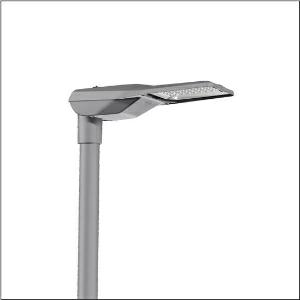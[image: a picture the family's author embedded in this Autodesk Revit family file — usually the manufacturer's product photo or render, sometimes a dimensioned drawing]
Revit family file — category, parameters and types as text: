
# Revit family: streetlight_sl_21_iq_mini___p0_5a_5xe2v31v08jb_ab6f
name_source: partatom
category: Lighting Fixtures
units: mm (PartAtom-declared; Revit-internal decimal feet)

## family parameters
Cut with Voids When Loaded = No
Host = Face
Light Source = No
Part Type = Normal
Room Calculation Point = No
Round Connector Dimension = Use Diameter
Shared = No

## types (1)
- --- (1 x LED, 11020 lm, 72.5 W, 3000K)
    Apparent Load = 73 VA
    CIE Flux Codes = 37 73 96 100 100
    Color Rendering = 70
    Color Temperature = 3000K
    Default Elevation = 1800 mm
    Description = Streetlight SL 21 iQ mini, mast luminaire, primary light control with lens, of PMMA, primary optical cover: cover, of toughened safety glass, transparent, light distribution: P0.5a, light emission: direct distribution, primary light characteristic: asymmetric, installation type: post-top, side-entry, LED, High Power LED, rated luminous flux: 11.020lm, luminous efficacy: 152lm/W, light colour: 730, colour temperature: 3000K, control gear: iQ-Street Remote, D4i with power reduction, control: pre-setting: logarithmic dimming characteristic, Street-Remote, Auto-Match, Temp-Guard, Lumen-Switch, Night-Set, Smart-Wire, Light-Fading, Desk-Remote (wireless, voltage-free reading and setting of iQ features in the workshop via application-optimized NFC function/RFID function), optimised constant luminous flux control (CLO 2.0), mains connection: 220..240V, AC, 50/60Hz, start of lifetime: 73W, end of service life: 76W, reduction: 33W, luminaire housing, of diecast aluminium, powder-coated, SITECO metallic grey (DB 702S), corrosivity category C5 high according to DIN EN ISO 12944, please order mast flange separately, inclination adjustable: 0°, 5°, 10°, 15°, sealing non-destructively replaceable, multi-level sealing system, length: 628mm, width: 235mm, height: 110mm, mast flange for spigot size: 42mm (side-entry): 5XC10008XM4, 60/48mm (side-entry/post-top): 5XC10108XM2, 76/60mm (side-entry/post-top): 5XC10108XM1, mounting height: 4..8m, Smart Interface above, protection rating (complete): IP66, insulation class (complete): insulation class II (safety insulation), certification: CE, ENEC, ENEC+, VDE, impact resistance: IK10, permissible operating ambient temperature for outdoor applications: -40..+50°C, standard-compliant lighting for roads and squares, packaging unit: 1 piece

Light Distribution: P0.5a
    Height = 110 mm
    Lamp = 1 x LED
    Lamp Light Flux = 11020 lm
    Lamp Power = 72.5 W
    Lamp count = 1
    Length = 625 mm
    Luminous efficacy = 152 lm/W
    Manufacturer = Siteco
    ModVariant = No
    Model = 5XE2V31V08JB
    Mounting Place = Pole
    Mounting Type = Pole top
    Number of Poles = 1
    OnlyDefault = Yes
    Power Factor = 1
    Product Name = Streetlight SL 21 iQ mini | P0.5a
    Product group = mast luminaire | pylon top
    ProductGroupID = 6100
    Protection Class = Protection class II
    Protection Degree = IP 66
    RLX_Detail_Level = 1
    RLX_Emergency_Light_Flux = 0 lm
    RLX_Emergency_Type = 0
    RLX_Emergency_Type_DB = No
    RlxData = <blob elided: 92185 chars, md5=e7a9c917>
    Socket = socket
    Standby Power = 0 W
    System Light Flux = 11020 lm
    System Power = 73 W
    Type Comments = factory setting: luminous flux: 100 % | dim-lin: 254 | 755 mA
    Type Image = l_1003515.jpg
    URL = http://relux.com
    VarID = @adj_078729
    Voltage = 0 V
    Weight = 0.00 kg
    Width = 234 mm

## geometry (parser evidence)
native form markers: Blend x4, Sweep x9
no freeform markers — native parametric forms only
